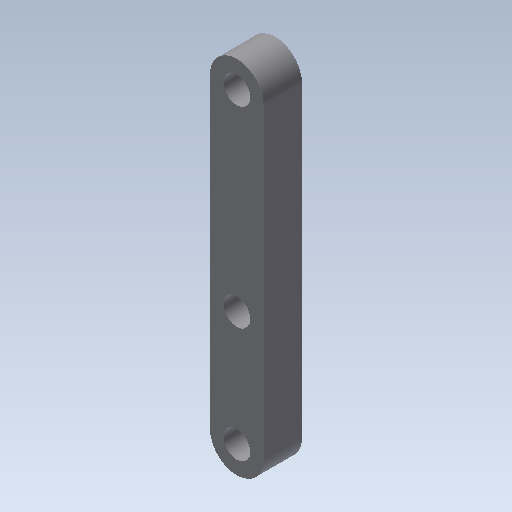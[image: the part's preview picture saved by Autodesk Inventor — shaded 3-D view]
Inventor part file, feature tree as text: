
AUTODESK INVENTOR PART (.ipt)
format: ipt  version: 2020.1 (Build 241239000, 239)  size: 102,400 bytes
history: native  units: mm
features: extrude x3, sketch x3
ambient origin geometry x8: Origin, YZ Plane, XZ Plane, XY Plane, X Axis, Y Axis, Z Axis, Center Point
bodies: Solid1 (feature_tree)
feature tree (6):
  extrude  "Extrusion1"  Depth=40.0mm
  extrude  "Extrusion2"  Depth=5.0mm TaperAngle=0.0deg
  extrude  "Extrusion3"  Depth=3.5mm
  sketch  "Sketch1"  dims[d0=7.0mm d1=40.0mm]
  sketch  "Sketch2"  dims[d2=7.0mm d3=5.0mm d4=0.0mm]
  sketch  "Sketch3"  dims[d5=3.5mm d6=3.5mm d7=5.0mm d8=0.0mm d9=15.0mm d10=3.5mm d11=10.0mm d12=0.0mm]
